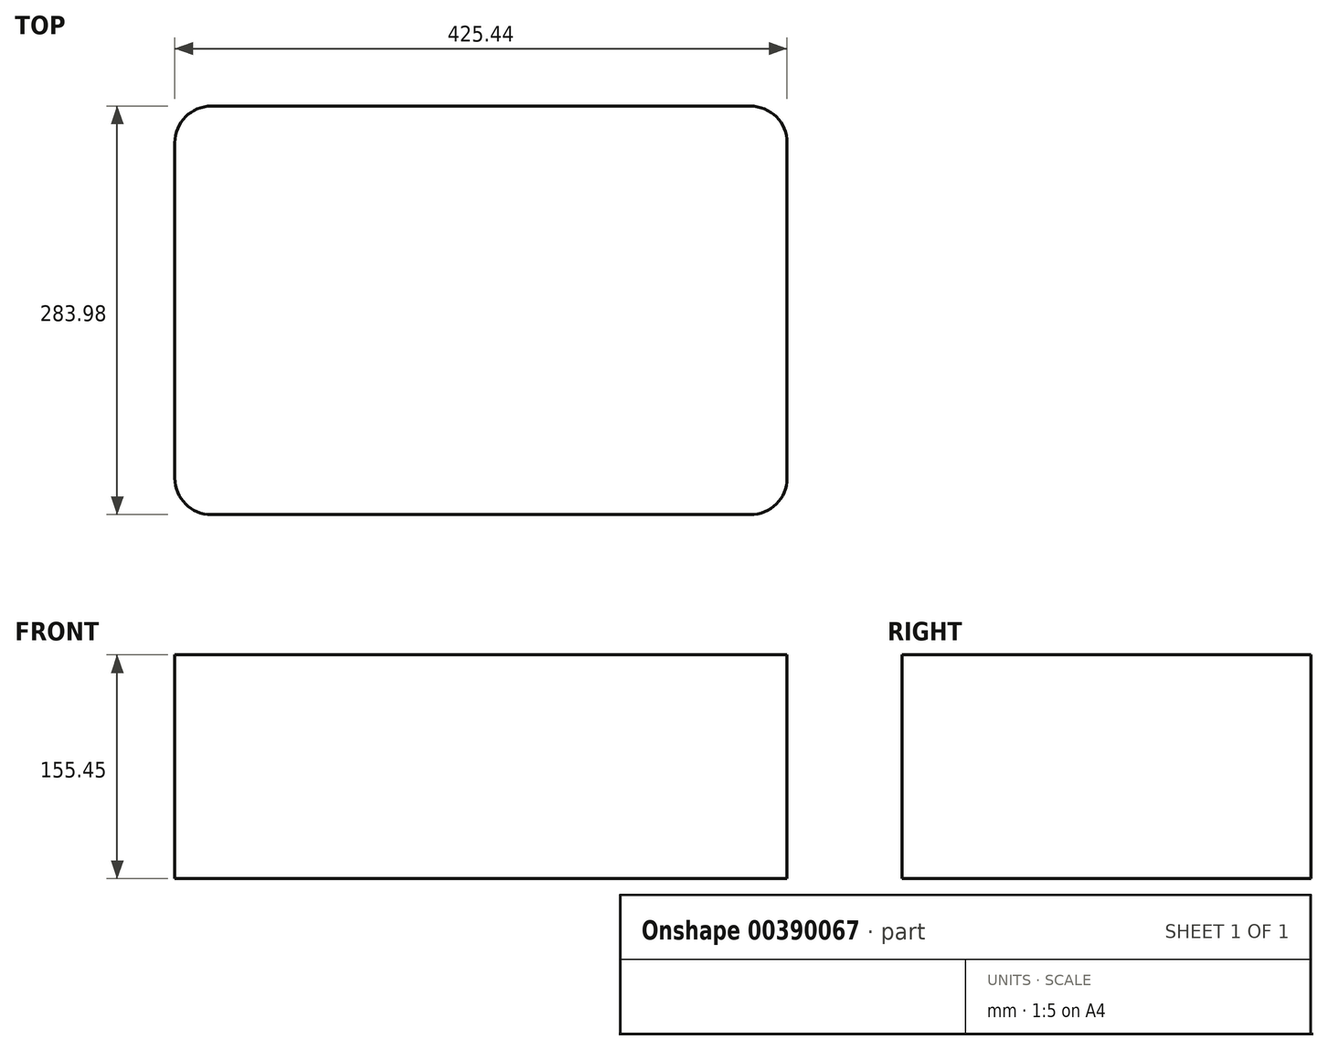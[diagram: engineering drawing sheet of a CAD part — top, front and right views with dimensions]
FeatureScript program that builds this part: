
annotation { "Feature Type Name" : "Feature", "Feature Type Description" : "" }
export const myFeature = defineFeature(function(context is Context, id is Id, definition is map)
    precondition{}
    {
        {
            var Q0;
            Q0=qCreatedBy(makeId("Top.planeOp"),FACE);
            var sketch = newSketch(context, id + "F0", { "sketchPlane" : qUnion([Q0])});
            skLineSegment(sketch, "E0.bottom", {"start": v(-187.32, 141.99) * mm, "end": v(187.32, 141.99) * mm});
            skLineSegment(sketch, "E0.top", {"start": v(-187.33, -141.99) * mm, "end": v(187.32, -141.99) * mm});
            skLineSegment(sketch, "E0.left", {"start": v(-212.72, 116.59) * mm, "end": v(-212.73, -116.59) * mm});
            skLineSegment(sketch, "E0.right", {"start": v(212.73, 116.59) * mm, "end": v(212.72, -116.59) * mm});
            skLineSegment(sketch, "E1", {"start": v(-212.72, 141.99) * mm, "end": v(212.73, -141.99) * mm, "construction": true});
            skPoint(sketch, "E2.visualSharp", {"position": v(-212.72, 141.99) * mm});
            skArc(sketch, "E2.filletArc", {"start": v(-187.32, 141.99) * mm, "mid": v(-205.29, 134.55) * mm, "end": v(-212.72, 116.59) * mm});
            skPoint(sketch, "E3.visualSharp", {"position": v(212.73, 141.99) * mm});
            skArc(sketch, "E3.filletArc", {"start": v(212.73, 116.59) * mm, "mid": v(205.29, 134.55) * mm, "end": v(187.32, 141.99) * mm});
            skPoint(sketch, "E4.visualSharp", {"position": v(212.72, -141.99) * mm});
            skArc(sketch, "E4.filletArc", {"start": v(187.32, -141.99) * mm, "mid": v(205.29, -134.55) * mm, "end": v(212.72, -116.59) * mm});
            skPoint(sketch, "E5.visualSharp", {"position": v(-212.73, -141.99) * mm});
            skArc(sketch, "E5.filletArc", {"start": v(-212.73, -116.59) * mm, "mid": v(-205.29, -134.55) * mm, "end": v(-187.33, -141.99) * mm});
            skSolve(sketch);
        }
        {
            var Q0;
            Q0=makeQuery(id+"F0.imprint","IMPRINT",FACE,{"disambiguationData":[TD([[makeQuery(id+"F0.imprint","IMPRINT",EDGE,{"derivedFrom":sQuery(id+"F0.wireOp",EDGE,"E0.bottom")}),-1.0]])]});
            extrude(context, id + "F1", {"entities" : qUnion([Q0]), "depth" : 155.45 * mm, "offsetDistance" : 25.4 * mm});
        }
    });
